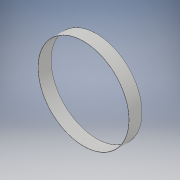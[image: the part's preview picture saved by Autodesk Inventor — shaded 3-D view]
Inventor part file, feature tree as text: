
AUTODESK INVENTOR PART (.ipt)
format: ipt  version: 2019 (Build 230136000, 136)  size: 104,448 bytes
history: native  units: mm
features: extrude x2, sketch x2
ambient origin geometry x8: Origin, YZ Plane, XZ Plane, XY Plane, X Axis, Y Axis, Z Axis, Center Point
bodies: Solid1 (feature_tree)
feature tree (4):
  extrude  "Extrusion1"  Depth=8.925mm TaperAngle=0.0deg
  extrude  "Extrusion2"  Depth=8.925mm TaperAngle=0.0deg
  sketch  "Sketch1"  dims[d0=62.9mm d1=8.925mm d2=0.0mm]
  sketch  "Sketch2"  dims[d3=62.6mm d4=8.925mm d5=0.0mm]
